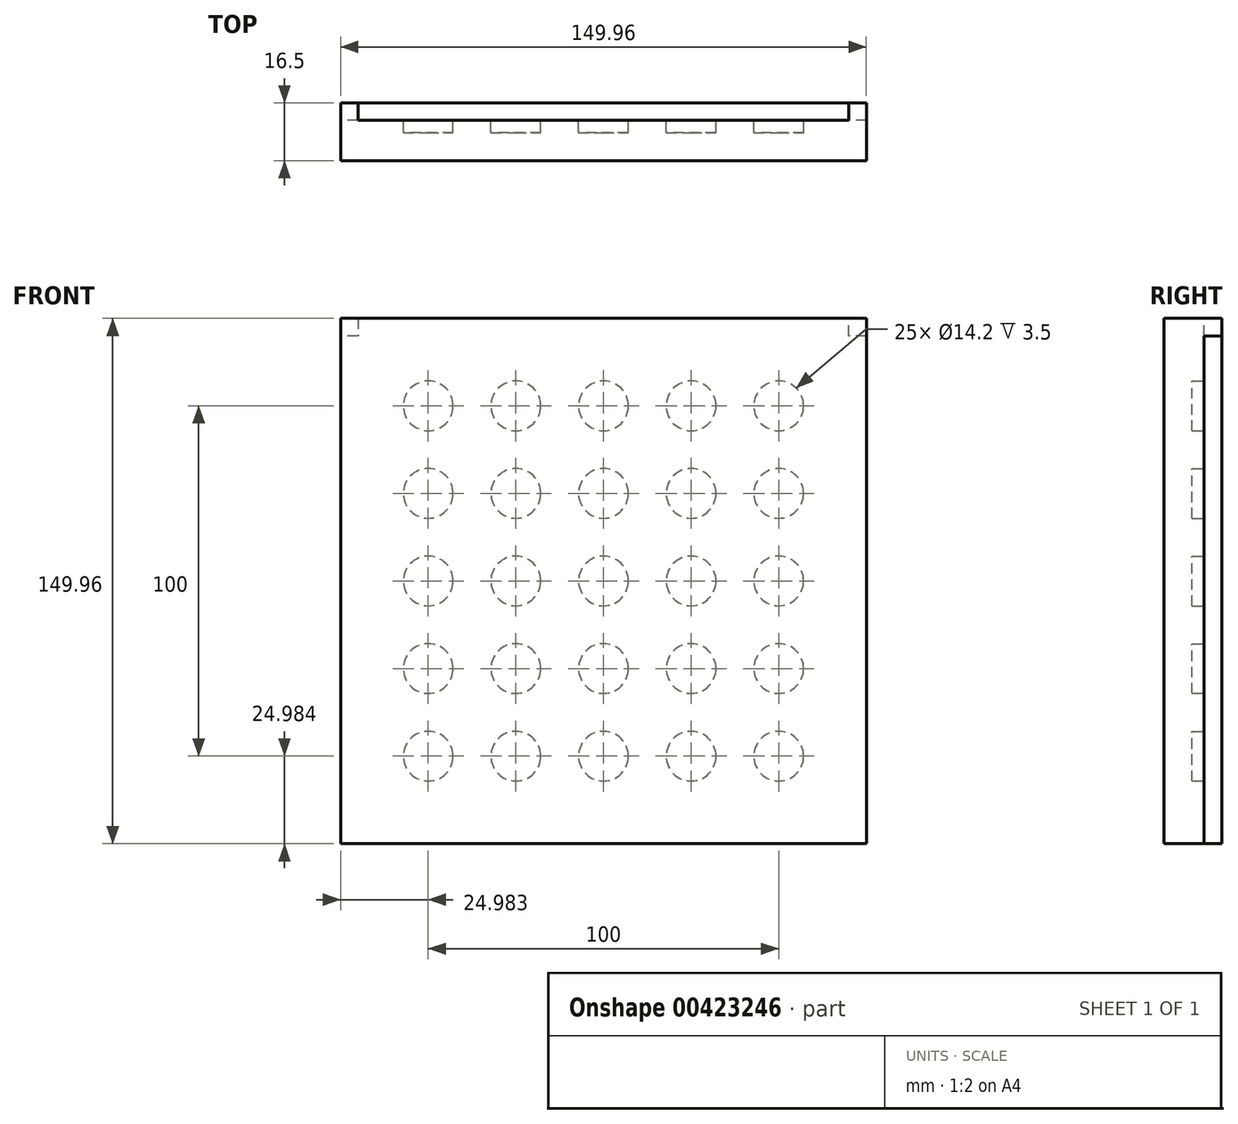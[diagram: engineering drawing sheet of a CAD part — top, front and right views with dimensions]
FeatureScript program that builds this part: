
annotation { "Feature Type Name" : "Feature", "Feature Type Description" : "" }
export const myFeature = defineFeature(function(context is Context, id is Id, definition is map)
    precondition{}
    {
        {
            var Q0;
            Q0=qCreatedBy(makeId("Front.planeOp"),FACE);
            var sketch = newSketch(context, id + "F0", { "sketchPlane" : qUnion([Q0])});
            skCircle(sketch, "E0", {"center": v(-61.1, 43.7) * mm, "radius": 7.1 * mm});
            skCircle(sketch, "E1.0.1.0", {"center": v(-61.1, 18.7) * mm, "radius": 7.1 * mm});
            skCircle(sketch, "E1.0.2.0", {"center": v(-61.1, -6.3) * mm, "radius": 7.1 * mm});
            skCircle(sketch, "E1.0.3.0", {"center": v(-61.1, -31.3) * mm, "radius": 7.1 * mm});
            skCircle(sketch, "E1.0.4.0", {"center": v(-61.1, -56.3) * mm, "radius": 7.1 * mm});
            skCircle(sketch, "E1.1.0.0", {"center": v(-36.1, 43.7) * mm, "radius": 7.1 * mm});
            skCircle(sketch, "E1.1.1.0", {"center": v(-36.1, 18.7) * mm, "radius": 7.1 * mm});
            skCircle(sketch, "E1.1.2.0", {"center": v(-36.1, -6.3) * mm, "radius": 7.1 * mm});
            skCircle(sketch, "E1.1.3.0", {"center": v(-36.1, -31.3) * mm, "radius": 7.1 * mm});
            skCircle(sketch, "E1.1.4.0", {"center": v(-36.1, -56.3) * mm, "radius": 7.1 * mm});
            skCircle(sketch, "E1.2.0.0", {"center": v(-11.1, 43.7) * mm, "radius": 7.1 * mm});
            skCircle(sketch, "E1.2.1.0", {"center": v(-11.1, 18.7) * mm, "radius": 7.1 * mm});
            skCircle(sketch, "E1.2.2.0", {"center": v(-11.1, -6.3) * mm, "radius": 7.1 * mm});
            skCircle(sketch, "E1.2.3.0", {"center": v(-11.1, -31.3) * mm, "radius": 7.1 * mm});
            skCircle(sketch, "E1.2.4.0", {"center": v(-11.1, -56.3) * mm, "radius": 7.1 * mm});
            skCircle(sketch, "E1.3.0.0", {"center": v(13.9, 43.7) * mm, "radius": 7.1 * mm});
            skCircle(sketch, "E1.3.1.0", {"center": v(13.9, 18.7) * mm, "radius": 7.1 * mm});
            skCircle(sketch, "E1.3.2.0", {"center": v(13.9, -6.3) * mm, "radius": 7.1 * mm});
            skCircle(sketch, "E1.3.3.0", {"center": v(13.9, -31.3) * mm, "radius": 7.1 * mm});
            skCircle(sketch, "E1.3.4.0", {"center": v(13.9, -56.3) * mm, "radius": 7.1 * mm});
            skCircle(sketch, "E1.4.0.0", {"center": v(38.9, 43.7) * mm, "radius": 7.1 * mm});
            skCircle(sketch, "E1.4.1.0", {"center": v(38.9, 18.7) * mm, "radius": 7.1 * mm});
            skCircle(sketch, "E1.4.2.0", {"center": v(38.9, -6.3) * mm, "radius": 7.1 * mm});
            skCircle(sketch, "E1.4.3.0", {"center": v(38.9, -31.3) * mm, "radius": 7.1 * mm});
            skCircle(sketch, "E1.4.4.0", {"center": v(38.9, -56.3) * mm, "radius": 7.1 * mm});
            skLineSegment(sketch, "E1.direction1", {"start": v(-61.1, 43.7) * mm, "end": v(-36.1, 43.7) * mm, "construction": true});
            skLineSegment(sketch, "E1.direction2", {"start": v(-61.1, 43.7) * mm, "end": v(-61.1, 18.7) * mm, "construction": true});
            skLineSegment(sketch, "E2", {"start": v(-11.1, -6.3) * mm, "end": v(-11.1, 100.02) * mm, "construction": true});
            skLineSegment(sketch, "E3", {"start": v(-11.1, -6.3) * mm, "end": v(76.39, -6.3) * mm, "construction": true});
            skLineSegment(sketch, "E4", {"start": v(58.88, 63.67) * mm, "end": v(-81.08, 63.67) * mm});
            skLineSegment(sketch, "E5", {"start": v(-81.08, 63.67) * mm, "end": v(-81.08, -76.29) * mm});
            skLineSegment(sketch, "E6", {"start": v(-81.08, -76.29) * mm, "end": v(58.88, -76.29) * mm});
            skLineSegment(sketch, "E7", {"start": v(58.88, 63.67) * mm, "end": v(58.88, -76.29) * mm});
            skSolve(sketch);
        }
        {
            var Q0;
            Q0=makeQuery(id+"F0.imprint","IMPRINT",FACE,{"disambiguationData":[TD([[makeQuery(id+"F0.imprint","IMPRINT",EDGE,{"derivedFrom":sQuery(id+"F0.wireOp",EDGE,"E0")}),-1.0]])]});
            extrude(context, id + "F1", {"entities" : qUnion([Q0]), "depth" : 3.5 * mm});
        }
        {
            var Q0;
            Q0=qCreatedBy(makeId("Front.planeOp"),FACE);
            cPlane(context, id + "F2", {"entities" : qUnion([Q0]), "cplaneType" : CPlaneType.OFFSET, "offset" : 3.5 * mm, "width" : 150 * mm, "height" : 150 * mm});
        }
        {
            var Q0;
            Q0=qCreatedBy(id+"F2.planeOp",FACE);
            var sketch = newSketch(context, id + "F3", { "sketchPlane" : qUnion([Q0])});
            skPoint(sketch, "E8.0", {"position": v(-81.08, 63.67) * mm});
            skPoint(sketch, "E9.0", {"position": v(58.88, 63.67) * mm});
            skPoint(sketch, "E10.0", {"position": v(58.88, -76.29) * mm});
            skPoint(sketch, "E11.0", {"position": v(-81.08, -76.29) * mm});
            skLineSegment(sketch, "E12", {"start": v(-81.08, 63.67) * mm, "end": v(58.88, 63.67) * mm});
            skLineSegment(sketch, "E13", {"start": v(58.88, 63.67) * mm, "end": v(58.88, -76.29) * mm});
            skLineSegment(sketch, "E14", {"start": v(58.88, -76.29) * mm, "end": v(-81.08, -76.29) * mm});
            skLineSegment(sketch, "E15", {"start": v(-81.08, -76.29) * mm, "end": v(-81.08, 63.67) * mm});
            skSolve(sketch);
        }
        {
            var Q0;
            Q0=makeQuery(id+"F3.imprint","IMPRINT",FACE,{"disambiguationData":[TD([[makeQuery(id+"F3.imprint","IMPRINT",EDGE,{"derivedFrom":sQuery(id+"F3.wireOp",EDGE,"E12")}),-1.0]])]});
            extrude(context, id + "F4", {"entities" : qUnion([Q0]), "depth" : 8 * mm});
        }
        {
            var Q0;
            Q0=makeQuery(id+"F4.opExtrude","CAP_FACE",FACE,{"disambiguationData":[OSD([sQuery(id+"F3.wireOp",EDGE,"E12"),sQuery(id+"F3.wireOp",EDGE,"E13"),sQuery(id+"F3.wireOp",EDGE,"E14"),sQuery(id+"F3.wireOp",EDGE,"E15")])],"isStart":false});
            cPlane(context, id + "F5", {"entities" : qUnion([Q0]), "cplaneType" : CPlaneType.OFFSET, "offset" : 0 * mm, "width" : 150 * mm, "height" : 150 * mm});
        }
        {
            var Q0;
            Q0=qCreatedBy(id+"F5.planeOp",FACE);
            var sketch = newSketch(context, id + "F6", { "sketchPlane" : qUnion([Q0])});
            skPoint(sketch, "E16.0", {"position": v(-81.08, 63.67) * mm});
            skPoint(sketch, "E17.0", {"position": v(58.88, 63.67) * mm});
            skPoint(sketch, "E18.0", {"position": v(58.88, -76.29) * mm});
            skPoint(sketch, "E19.0", {"position": v(-81.08, -76.29) * mm});
            skLineSegment(sketch, "E20", {"start": v(-81.08, 63.67) * mm, "end": v(58.88, 63.67) * mm});
            skLineSegment(sketch, "E21", {"start": v(58.88, 63.67) * mm, "end": v(58.88, -76.29) * mm});
            skLineSegment(sketch, "E22", {"start": v(58.88, -76.29) * mm, "end": v(63.88, -76.29) * mm});
            skLineSegment(sketch, "E23", {"start": v(63.88, -76.29) * mm, "end": v(63.88, 68.67) * mm});
            skLineSegment(sketch, "E24", {"start": v(63.88, 68.67) * mm, "end": v(-86.08, 68.67) * mm});
            skLineSegment(sketch, "E25", {"start": v(-86.08, 68.67) * mm, "end": v(-86.08, -76.29) * mm});
            skLineSegment(sketch, "E26", {"start": v(-86.08, -76.29) * mm, "end": v(-81.08, -76.29) * mm});
            skLineSegment(sketch, "E27", {"start": v(-81.08, -76.29) * mm, "end": v(-81.08, 63.67) * mm});
            skSolve(sketch);
        }
        {
            var Q0;
            Q0=makeQuery(id+"F6.imprint","IMPRINT",FACE,{"disambiguationData":[TD([[makeQuery(id+"F6.imprint","IMPRINT",EDGE,{"derivedFrom":sQuery(id+"F6.wireOp",EDGE,"E20")}),1.0]])]});
            extrude(context, id + "F7", {"entities" : qUnion([Q0]), "operationType" : NewBodyOperationType.ADD, "oppositeDirection" : true, "depth" : 11.5 * mm});
        }
        {
            var Q0;
            Q0=qCreatedBy(makeId("Front.planeOp"),FACE);
            var sketch = newSketch(context, id + "F8", { "sketchPlane" : qUnion([Q0])});
            skPoint(sketch, "E28.0", {"position": v(-86.08, -76.29) * mm});
            skPoint(sketch, "E29.0", {"position": v(63.88, -76.29) * mm});
            skLineSegment(sketch, "E30", {"start": v(-86.08, -76.29) * mm, "end": v(63.88, -76.29) * mm});
            skLineSegment(sketch, "E31", {"start": v(63.88, -76.29) * mm, "end": v(63.88, -81.29) * mm});
            skLineSegment(sketch, "E32", {"start": v(63.88, -81.29) * mm, "end": v(-86.08, -81.29) * mm});
            skLineSegment(sketch, "E33", {"start": v(-86.08, -81.29) * mm, "end": v(-86.08, -76.29) * mm});
            skSolve(sketch);
        }
        {
            var Q0;
            Q0=makeQuery(id+"F8.imprint","IMPRINT",FACE,{"disambiguationData":[TD([[makeQuery(id+"F8.imprint","IMPRINT",EDGE,{"derivedFrom":sQuery(id+"F8.wireOp",EDGE,"E30")}),-1.0]])]});
            extrude(context, id + "F9", {"entities" : qUnion([Q0]), "operationType" : NewBodyOperationType.ADD, "depth" : 11.5 * mm});
        }
        {
            var Q0;
            Q0=qCreatedBy(makeId("Front.planeOp"),FACE);
            var sketch = newSketch(context, id + "F10", { "sketchPlane" : qUnion([Q0])});
            skPoint(sketch, "E34.0", {"position": v(63.88, 68.67) * mm});
            skPoint(sketch, "E35.0", {"position": v(-86.08, 68.67) * mm});
            skPoint(sketch, "E36.0", {"position": v(-86.08, -81.29) * mm});
            skPoint(sketch, "E37.0", {"position": v(63.88, -81.29) * mm});
            skPoint(sketch, "E38.0", {"position": v(58.88, 63.67) * mm});
            skPoint(sketch, "E39.0", {"position": v(-81.08, 63.67) * mm});
            skLineSegment(sketch, "E40.bottom", {"start": v(63.88, 68.67) * mm, "end": v(58.88, 68.67) * mm});
            skLineSegment(sketch, "E40.top", {"start": v(63.88, 63.67) * mm, "end": v(58.88, 63.67) * mm});
            skLineSegment(sketch, "E40.left", {"start": v(63.88, 68.67) * mm, "end": v(63.88, 63.67) * mm});
            skLineSegment(sketch, "E40.right", {"start": v(58.88, 68.67) * mm, "end": v(58.88, 63.67) * mm});
            skLineSegment(sketch, "E41.bottom", {"start": v(-81.08, 63.67) * mm, "end": v(-86.08, 63.67) * mm});
            skLineSegment(sketch, "E41.top", {"start": v(-81.08, 68.67) * mm, "end": v(-86.08, 68.67) * mm});
            skLineSegment(sketch, "E41.left", {"start": v(-81.08, 63.67) * mm, "end": v(-81.08, 68.67) * mm});
            skLineSegment(sketch, "E41.right", {"start": v(-86.08, 63.67) * mm, "end": v(-86.08, 68.67) * mm});
            skSolve(sketch);
        }
        {
            var Q0;
            Q0=makeQuery(id+"F10.imprint","IMPRINT",FACE,{"disambiguationData":[TD([[makeQuery(id+"F10.imprint","IMPRINT",EDGE,{"derivedFrom":sQuery(id+"F10.wireOp",EDGE,"E41.bottom")}),-1.0]])]});
            var Q1;
            Q1=makeQuery(id+"F10.imprint","IMPRINT",FACE,{"disambiguationData":[TD([[makeQuery(id+"F10.imprint","IMPRINT",EDGE,{"derivedFrom":sQuery(id+"F10.wireOp",EDGE,"E40.bottom")}),1.0]])]});
            extrude(context, id + "F11", {"entities" : qUnion([Q0, Q1]), "operationType" : NewBodyOperationType.ADD, "oppositeDirection" : true, "depth" : 5 * mm});
        }
        {
            var Q0;
            Q0=qCreatedBy(makeId("Front.planeOp"),FACE);
            var sketch = newSketch(context, id + "F12", { "sketchPlane" : qUnion([Q0])});
            skPoint(sketch, "E42.0", {"position": v(63.88, 68.67) * mm});
            skPoint(sketch, "E43.0", {"position": v(58.88, 63.67) * mm});
            skPoint(sketch, "E44.0", {"position": v(58.88, 68.67) * mm});
            skPoint(sketch, "E45.0", {"position": v(63.88, 63.67) * mm});
            skPoint(sketch, "E46.0", {"position": v(-81.08, 68.67) * mm});
            skPoint(sketch, "E47.0", {"position": v(-81.08, 63.67) * mm});
            skPoint(sketch, "E48.0", {"position": v(-86.08, 63.67) * mm});
            skPoint(sketch, "E49.0", {"position": v(-86.08, -81.29) * mm});
            skPoint(sketch, "E50.0", {"position": v(63.88, -81.29) * mm});
            skLineSegment(sketch, "E51", {"start": v(58.88, 68.67) * mm, "end": v(-81.08, 68.67) * mm});
            skLineSegment(sketch, "E52", {"start": v(-81.08, 68.67) * mm, "end": v(-81.08, 63.67) * mm});
            skLineSegment(sketch, "E53", {"start": v(-81.08, 63.67) * mm, "end": v(-86.08, 63.67) * mm});
            skLineSegment(sketch, "E54", {"start": v(-86.08, 63.67) * mm, "end": v(-86.08, -81.29) * mm});
            skLineSegment(sketch, "E55", {"start": v(-86.08, -81.29) * mm, "end": v(63.88, -81.29) * mm});
            skLineSegment(sketch, "E56", {"start": v(63.88, -81.29) * mm, "end": v(63.88, 63.67) * mm});
            skLineSegment(sketch, "E57", {"start": v(63.88, 63.67) * mm, "end": v(58.88, 63.67) * mm});
            skLineSegment(sketch, "E58", {"start": v(58.88, 63.67) * mm, "end": v(58.88, 68.67) * mm});
            skSolve(sketch);
        }
        {
            var Q0;
            Q0=qSketchRegion(id+"F12",true);
            extrude(context, id + "F13", {"entities" : qUnion([Q0]), "oppositeDirection" : true, "depth" : 5 * mm});
        }
    });
